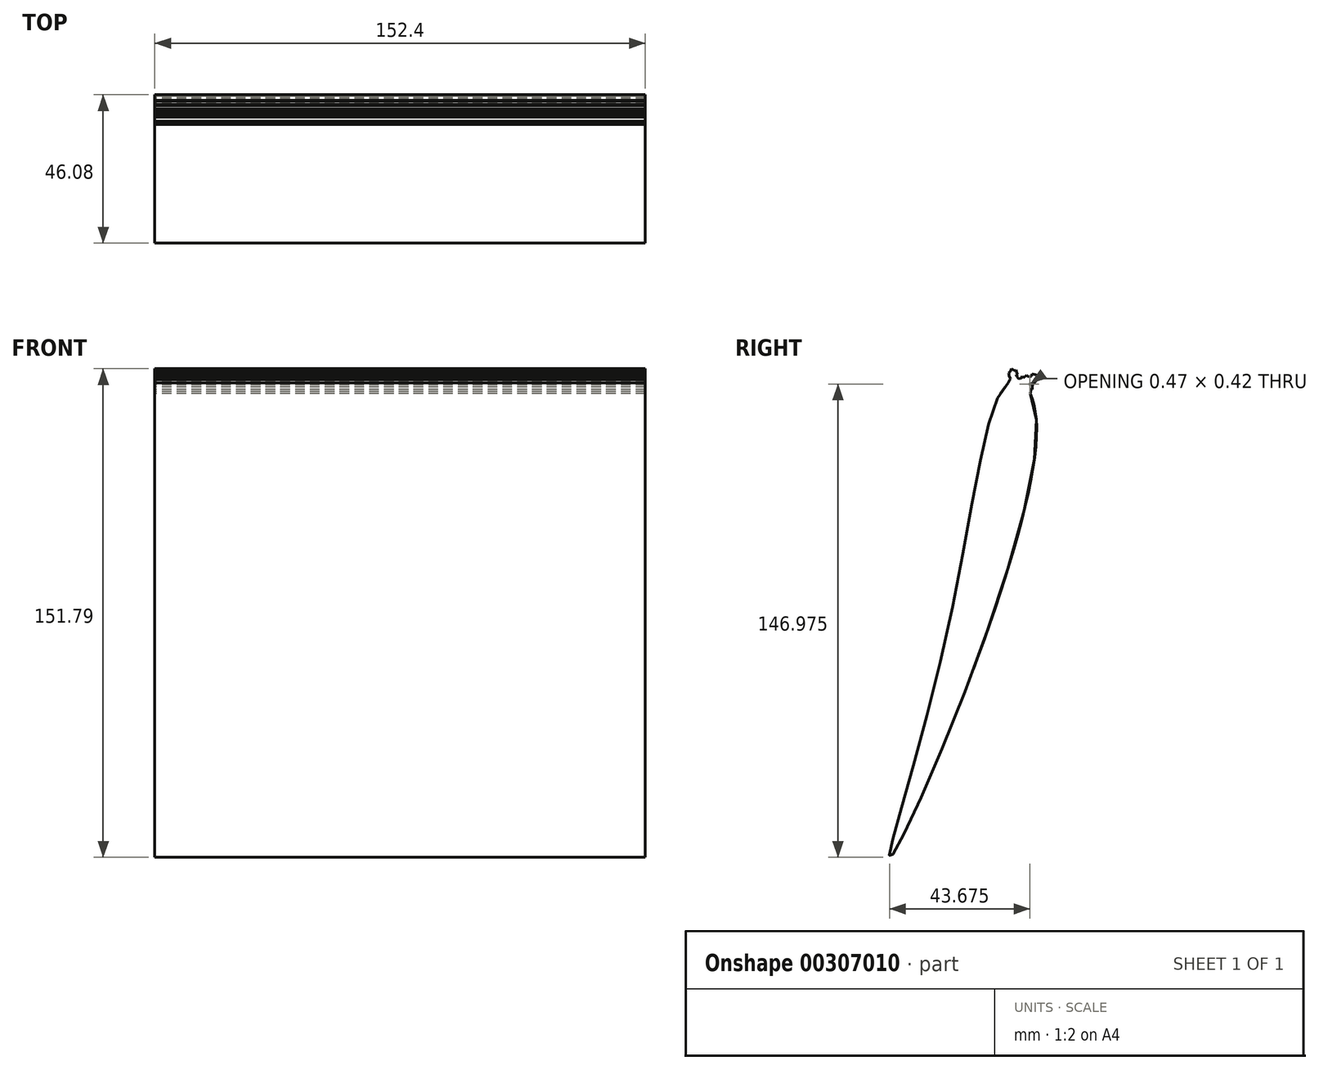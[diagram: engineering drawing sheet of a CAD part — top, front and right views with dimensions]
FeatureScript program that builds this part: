
annotation { "Feature Type Name" : "Feature", "Feature Type Description" : "" }
export const myFeature = defineFeature(function(context is Context, id is Id, definition is map)
    precondition{}
    {
        {
            var Q0;
            Q0=qCreatedBy(makeId("Right.planeOp"),FACE);
            var sketch = newSketch(context, id + "F0", { "sketchPlane" : qUnion([Q0])});
            skFitSpline(sketch, "E0", {"points": [v(34.7, 70.83) * mm, v(42.97, 55.32) * mm, v(-2.03, -76.46) * mm, v(14.34, -10.78) * mm, v(34.7, 70.83) * mm]});
            skLineSegment(sketch, "E1", {"start": v(38.76, 70.2) * mm, "end": v(41.6, 72.44) * mm});
            skLineSegment(sketch, "E2", {"start": v(41.6, 72.44) * mm, "end": v(42.47, 71.48) * mm});
            skLineSegment(sketch, "E3", {"start": v(42.47, 71.48) * mm, "end": v(39.8, 69.08) * mm});
            skLineSegment(sketch, "E4", {"start": v(39.8, 69.08) * mm, "end": v(38.76, 70.2) * mm});
            skLineSegment(sketch, "E5", {"start": v(41.6, 72.44) * mm, "end": v(42.32, 73.08) * mm});
            skPoint(sketch, "E5.endSnap0", {"position": v(42.04, 71.96) * mm});
            skLineSegment(sketch, "E6", {"start": v(42.32, 73.08) * mm, "end": v(43.12, 72.06) * mm});
            skLineSegment(sketch, "E7", {"start": v(43.12, 72.06) * mm, "end": v(42.47, 71.48) * mm});
            skLineSegment(sketch, "E8", {"start": v(36.46, 71.21) * mm, "end": v(36.05, 73.82) * mm});
            skLineSegment(sketch, "E9", {"start": v(36.05, 73.82) * mm, "end": v(34.77, 73.62) * mm});
            skLineSegment(sketch, "E10", {"start": v(34.77, 73.62) * mm, "end": v(35.17, 71.04) * mm});
            skLineSegment(sketch, "E11", {"start": v(35.17, 71.04) * mm, "end": v(36.46, 71.21) * mm});
            skLineSegment(sketch, "E12", {"start": v(40.32, 68.46) * mm, "end": v(40.67, 69.85) * mm});
            skLineSegment(sketch, "E13", {"start": v(40.67, 69.85) * mm, "end": v(41.14, 70.28) * mm});
            skLineSegment(sketch, "E14", {"start": v(41.14, 70.28) * mm, "end": v(41.08, 70.02) * mm});
            skPoint(sketch, "E14.endSnap0", {"position": v(40.9, 70.07) * mm});
            skLineSegment(sketch, "E15", {"start": v(41.08, 70.02) * mm, "end": v(40.67, 69.85) * mm});
            skLineSegment(sketch, "E16", {"start": v(40.5, 69.16) * mm, "end": v(41.26, 69.84) * mm});
            skLineSegment(sketch, "E17", {"start": v(41.26, 69.84) * mm, "end": v(41.43, 70.54) * mm});
            skLineSegment(sketch, "E18", {"start": v(41.43, 70.54) * mm, "end": v(41.8, 70.12) * mm});
            skLineSegment(sketch, "E19", {"start": v(41.8, 70.12) * mm, "end": v(41.26, 69.84) * mm});
            skLineSegment(sketch, "E20", {"start": v(42.1, 71.14) * mm, "end": v(42.93, 70.94) * mm});
            skLineSegment(sketch, "E21", {"start": v(42.93, 70.94) * mm, "end": v(42.47, 71.48) * mm});
            skLineSegment(sketch, "E22", {"start": v(43.12, 72.06) * mm, "end": v(43.03, 71.34) * mm});
            skLineSegment(sketch, "E23", {"start": v(43.03, 71.34) * mm, "end": v(42.27, 70.66) * mm});
            skLineSegment(sketch, "E24", {"start": v(42.27, 70.66) * mm, "end": v(41.43, 70.54) * mm});
            skLineSegment(sketch, "E25", {"start": v(42.27, 70.66) * mm, "end": v(42.2, 70.35) * mm});
            skLineSegment(sketch, "E26", {"start": v(42.2, 70.35) * mm, "end": v(41.8, 70.12) * mm});
            skLineSegment(sketch, "E27", {"start": v(43.03, 71.34) * mm, "end": v(42.47, 71.48) * mm});
            skLineSegment(sketch, "E28", {"start": v(41.8, 70.12) * mm, "end": v(41.57, 69.17) * mm});
            skLineSegment(sketch, "E29", {"start": v(41.57, 69.17) * mm, "end": v(40.5, 69.16) * mm});
            skLineSegment(sketch, "E30", {"start": v(43.12, 72.06) * mm, "end": v(43.31, 72.83) * mm});
            skLineSegment(sketch, "E31", {"start": v(43.31, 72.83) * mm, "end": v(42.85, 72.4) * mm});
            skLineSegment(sketch, "E32", {"start": v(42.85, 72.4) * mm, "end": v(43.31, 72.83) * mm});
            skLineSegment(sketch, "E33", {"start": v(43.31, 72.83) * mm, "end": v(42.32, 73.08) * mm});
            skLineSegment(sketch, "E34", {"start": v(42.32, 73.08) * mm, "end": v(41.52, 73.28) * mm});
            skLineSegment(sketch, "E35", {"start": v(41.52, 73.28) * mm, "end": v(41.33, 72.5) * mm});
            skLineSegment(sketch, "E36", {"start": v(41.33, 72.5) * mm, "end": v(40.33, 72.38) * mm});
            skLineSegment(sketch, "E37", {"start": v(40.33, 72.38) * mm, "end": v(39.9, 72.86) * mm});
            skLineSegment(sketch, "E38", {"start": v(39.9, 72.86) * mm, "end": v(39.62, 71.76) * mm});
            skLineSegment(sketch, "E39", {"start": v(39.62, 71.76) * mm, "end": v(39.52, 71.34) * mm});
            skLineSegment(sketch, "E40", {"start": v(39.52, 71.34) * mm, "end": v(38.78, 71.34) * mm});
            skLineSegment(sketch, "E41", {"start": v(38.78, 71.34) * mm, "end": v(38.56, 70.47) * mm});
            skLineSegment(sketch, "E42", {"start": v(38.56, 70.47) * mm, "end": v(38.76, 70.2) * mm});
            skLineSegment(sketch, "E43", {"start": v(39.9, 72.86) * mm, "end": v(38.88, 71.95) * mm});
            skLineSegment(sketch, "E44", {"start": v(38.88, 71.95) * mm, "end": v(38.39, 72.5) * mm});
            skLineSegment(sketch, "E45", {"start": v(38.39, 72.5) * mm, "end": v(37.95, 71.74) * mm});
            skLineSegment(sketch, "E46", {"start": v(37.95, 71.74) * mm, "end": v(37.25, 71.9) * mm});
            skLineSegment(sketch, "E47", {"start": v(37.25, 71.9) * mm, "end": v(36.66, 71.36) * mm});
            skLineSegment(sketch, "E48", {"start": v(37.25, 71.9) * mm, "end": v(36.73, 72.48) * mm});
            skLineSegment(sketch, "E49", {"start": v(36.73, 72.48) * mm, "end": v(36.35, 72.13) * mm});
            skLineSegment(sketch, "E50", {"start": v(36.35, 72.13) * mm, "end": v(36.55, 72.95) * mm});
            skLineSegment(sketch, "E51", {"start": v(36.55, 72.95) * mm, "end": v(36.12, 73.43) * mm});
            skLineSegment(sketch, "E52", {"start": v(36.12, 73.43) * mm, "end": v(36.05, 73.82) * mm});
            skLineSegment(sketch, "E53", {"start": v(36.55, 72.95) * mm, "end": v(36.73, 73.65) * mm});
            skLineSegment(sketch, "E54", {"start": v(36.73, 73.65) * mm, "end": v(36.12, 73.43) * mm});
            skLineSegment(sketch, "E55", {"start": v(36.73, 73.65) * mm, "end": v(37.16, 73.17) * mm});
            skLineSegment(sketch, "E56", {"start": v(37.16, 73.17) * mm, "end": v(36.55, 72.95) * mm});
            skLineSegment(sketch, "E57", {"start": v(36.73, 73.65) * mm, "end": v(36.6, 74.5) * mm});
            skLineSegment(sketch, "E58", {"start": v(36.6, 74.5) * mm, "end": v(36.05, 73.82) * mm});
            skLineSegment(sketch, "E59", {"start": v(36.05, 73.82) * mm, "end": v(35.57, 74.36) * mm});
            skPoint(sketch, "E59.endSnap0", {"position": v(35.4, 73.72) * mm});
            skLineSegment(sketch, "E60", {"start": v(35.57, 74.36) * mm, "end": v(34.77, 73.62) * mm});
            skLineSegment(sketch, "E61", {"start": v(34.77, 73.62) * mm, "end": v(35.08, 74.88) * mm});
            skLineSegment(sketch, "E62", {"start": v(35.08, 74.88) * mm, "end": v(36.32, 74.16) * mm});
            skLineSegment(sketch, "E63", {"start": v(36.32, 74.16) * mm, "end": v(36.6, 74.5) * mm});
            skLineSegment(sketch, "E64", {"start": v(34.89, 74.11) * mm, "end": v(34.24, 73.53) * mm});
            skLineSegment(sketch, "E65", {"start": v(34.24, 73.53) * mm, "end": v(35.01, 72.14) * mm});
            skLineSegment(sketch, "E66", {"start": v(35.01, 72.14) * mm, "end": v(34.4, 72.62) * mm});
            skLineSegment(sketch, "E67", {"start": v(34.4, 72.62) * mm, "end": v(34.34, 73.08) * mm});
            skLineSegment(sketch, "E68", {"start": v(34.34, 73.08) * mm, "end": v(34.24, 73.53) * mm});
            skLineSegment(sketch, "E69", {"start": v(35.17, 71.04) * mm, "end": v(34.7, 70.83) * mm});
            skLineSegment(sketch, "E70", {"start": v(34.7, 70.83) * mm, "end": v(34.59, 71.5) * mm});
            skLineSegment(sketch, "E71", {"start": v(34.59, 71.5) * mm, "end": v(35.07, 72.04) * mm});
            skLineSegment(sketch, "E72", {"start": v(35.07, 72.04) * mm, "end": v(34.4, 72.62) * mm});
            skLineSegment(sketch, "E73", {"start": v(34.4, 72.62) * mm, "end": v(34.83, 71.77) * mm});
            skLineSegment(sketch, "E74", {"start": v(41.57, 69.17) * mm, "end": v(41.58, 68.47) * mm});
            skLineSegment(sketch, "E75", {"start": v(41.58, 68.47) * mm, "end": v(41.05, 68.4) * mm});
            skLineSegment(sketch, "E76", {"start": v(41.05, 68.4) * mm, "end": v(41.13, 67.78) * mm});
            skLineSegment(sketch, "E77", {"start": v(41.13, 67.78) * mm, "end": v(40.97, 67.13) * mm});
            skLineSegment(sketch, "E78", {"start": v(40.97, 67.13) * mm, "end": v(40.32, 68.46) * mm});
            skLineSegment(sketch, "E79", {"start": v(34.59, 71.5) * mm, "end": v(34.08, 70.44) * mm});
            skLineSegment(sketch, "E80", {"start": v(34.08, 70.44) * mm, "end": v(34.7, 70.83) * mm});
            skLineSegment(sketch, "E81", {"start": v(36.55, 72.95) * mm, "end": v(36.73, 72.48) * mm});
            skLineSegment(sketch, "E82.0", {"start": v(34.59, 71.5) * mm, "end": v(41.26, 69.84) * mm, "construction": true});
            skLineSegment(sketch, "E83.0", {"start": v(34.34, 73.08) * mm, "end": v(42.93, 70.94) * mm, "construction": true});
            skLineSegment(sketch, "E84.0", {"start": v(34.4, 72.62) * mm, "end": v(37.25, 71.9) * mm, "construction": true});
            skLineSegment(sketch, "E85.0", {"start": v(35.01, 72.14) * mm, "end": v(42.2, 70.35) * mm, "construction": true});
            skLineSegment(sketch, "E86.0", {"start": v(34.24, 73.53) * mm, "end": v(43.03, 71.34) * mm, "construction": true});
            skLineSegment(sketch, "E87.0", {"start": v(35.08, 74.88) * mm, "end": v(43.31, 72.83) * mm, "construction": true});
            skLineSegment(sketch, "E88.0", {"start": v(34.89, 74.11) * mm, "end": v(43.12, 72.06) * mm, "construction": true});
            skLineSegment(sketch, "E89.0", {"start": v(36.12, 73.43) * mm, "end": v(42.04, 71.96) * mm, "construction": true});
            skLineSegment(sketch, "E90.0", {"start": v(40.9, 70.07) * mm, "end": v(41.08, 70.02) * mm, "construction": true});
            skLineSegment(sketch, "E91.0", {"start": v(38.88, 71.95) * mm, "end": v(39.62, 71.76) * mm, "construction": true});
            skLineSegment(sketch, "E92.0", {"start": v(39.52, 71.34) * mm, "end": v(42.27, 70.66) * mm, "construction": true});
            skLineSegment(sketch, "E93.0", {"start": v(35.01, 72.14) * mm, "end": v(35.57, 74.36) * mm, "construction": true});
            skLineSegment(sketch, "E94.0", {"start": v(42.27, 70.66) * mm, "end": v(42.47, 71.48) * mm, "construction": true});
            skLineSegment(sketch, "E95.0", {"start": v(34.77, 73.62) * mm, "end": v(34.89, 74.11) * mm, "construction": true});
            skLineSegment(sketch, "E96.0", {"start": v(42.04, 71.96) * mm, "end": v(42.32, 73.08) * mm, "construction": true});
            skLineSegment(sketch, "E97.0", {"start": v(40.5, 69.16) * mm, "end": v(41.52, 73.28) * mm, "construction": true});
            skLineSegment(sketch, "E98.0", {"start": v(42.93, 70.94) * mm, "end": v(43.03, 71.34) * mm, "construction": true});
            skSolve(sketch);
        }
        {
            var Q0;
            Q0=qSketchRegion(id+"F0",true);
            var Q1;
            Q1=makeQuery(id+"F0.imprint","IMPRINT",FACE,{"disambiguationData":[TD([[makeQuery(id+"F0.imprint","IMPRINT",EDGE,{"derivedFrom":sQuery(id+"F0.wireOp",EDGE,"E1")}),1.0]])]});
            var Q2;
            {var subQ3=sQuery(id+"F0.wireOp",EDGE,"E1");Q2=makeQuery(id+"F0.imprint","IMPRINT",FACE,{"disambiguationData":[TD([[makeQuery(id+"F0.imprint","IMPRINT",EDGE,{"derivedFrom":subQ3}),-1.0]])]});}
            var Q3;
            {var subQ0=sQuery(id+"F0.wireOp",EDGE,"E29");Q3=makeQuery(id+"F0.imprint","IMPRINT",FACE,{"disambiguationData":[TD([[makeQuery(id+"F0.imprint","IMPRINT",EDGE,{"derivedFrom":subQ0}),1.0]])]});}
            var Q4;
            {var subQ0=sQuery(id+"F0.wireOp",EDGE,"E78");var subQ1=sQuery(id+"F0.wireOp",EDGE,"E12");var subQ2=makeQuery(id+"F0.imprint","INTERSECT",VERTEX,{"derivedFrom":[subQ1,subQ0]});Q4=makeQuery(id+"F0.imprint","IMPRINT",FACE,{"disambiguationData":[TD([[makeQuery(id+"F0.imprint","IMPRINT",EDGE,{"disambiguationData":[TD([[subQ2,1.0]])],"derivedFrom":subQ0}),1.0]])]});}
            var Q5;
            {var subQ2=sQuery(id+"F0.wireOp",EDGE,"E8");Q5=makeQuery(id+"F0.imprint","IMPRINT",FACE,{"disambiguationData":[TD([[makeQuery(id+"F0.imprint","IMPRINT",EDGE,{"derivedFrom":subQ2}),-1.0]])]});}
            var Q6;
            {var subQ0=sQuery(id+"F0.wireOp",EDGE,"E11");Q6=makeQuery(id+"F0.imprint","IMPRINT",FACE,{"disambiguationData":[TD([[makeQuery(id+"F0.imprint","IMPRINT",EDGE,{"derivedFrom":subQ0}),1.0]])]});}
            var Q7;
            {var subQ0=sQuery(id+"F0.wireOp",EDGE,"E4");Q7=makeQuery(id+"F0.imprint","IMPRINT",FACE,{"disambiguationData":[TD([[makeQuery(id+"F0.imprint","IMPRINT",EDGE,{"derivedFrom":subQ0}),-1.0]])]});}
            var Q8;
            {var subQ0=sQuery(id+"F0.wireOp",EDGE,"E78");var subQ1=sQuery(id+"F0.wireOp",EDGE,"E0");var subQ3=makeQuery(id+"F0.imprint","INTERSECT",VERTEX,{"derivedFrom":[subQ1,subQ0]});Q8=makeQuery(id+"F0.imprint","IMPRINT",FACE,{"disambiguationData":[TD([[makeQuery(id+"F0.imprint","IMPRINT",EDGE,{"disambiguationData":[TD([[subQ3,-1.0]])],"derivedFrom":subQ1}),-1.0]])]});}
            var Q9;
            {var subQ6=sQuery(id+"F0.wireOp",EDGE,"E8");Q9=makeQuery(id+"F0.imprint","IMPRINT",FACE,{"disambiguationData":[TD([[makeQuery(id+"F0.imprint","IMPRINT",EDGE,{"derivedFrom":subQ6}),1.0]])]});}
            var Q10;
            Q10=makeQuery(id+"F0.imprint","IMPRINT",FACE,{"disambiguationData":[TD([[makeQuery(id+"F0.imprint","IMPRINT",EDGE,{"derivedFrom":sQuery(id+"F0.wireOp",EDGE,"E58")}),-1.0]])]});
            var Q11;
            {var subQ0=sQuery(id+"F0.wireOp",EDGE,"E69");Q11=makeQuery(id+"F0.imprint","IMPRINT",FACE,{"disambiguationData":[TD([[makeQuery(id+"F0.imprint","IMPRINT",EDGE,{"derivedFrom":subQ0}),-1.0]])]});}
            var Q12;
            {var subQ1=sQuery(id+"F0.wireOp",EDGE,"E70");Q12=makeQuery(id+"F0.imprint","IMPRINT",FACE,{"disambiguationData":[TD([[makeQuery(id+"F0.imprint","IMPRINT",EDGE,{"derivedFrom":subQ1}),1.0]])]});}
            var Q13;
            {var subQ0=sQuery(id+"F0.wireOp",EDGE,"E80");Q13=makeQuery(id+"F0.imprint","IMPRINT",FACE,{"disambiguationData":[TD([[makeQuery(id+"F0.imprint","IMPRINT",EDGE,{"derivedFrom":subQ0}),1.0]])]});}
            var Q14;
            {var subQ5=sQuery(id+"F0.wireOp",EDGE,"E64");Q14=makeQuery(id+"F0.imprint","IMPRINT",FACE,{"disambiguationData":[TD([[makeQuery(id+"F0.imprint","IMPRINT",EDGE,{"derivedFrom":subQ5}),1.0]])]});}
            var Q15;
            {var subQ1=sQuery(id+"F0.wireOp",EDGE,"E70");Q15=makeQuery(id+"F0.imprint","IMPRINT",FACE,{"disambiguationData":[TD([[makeQuery(id+"F0.imprint","IMPRINT",EDGE,{"derivedFrom":subQ1}),-1.0]])]});}
            var Q16;
            {var subQ0=sQuery(id+"F0.wireOp",EDGE,"E67");Q16=makeQuery(id+"F0.imprint","IMPRINT",FACE,{"disambiguationData":[TD([[makeQuery(id+"F0.imprint","IMPRINT",EDGE,{"derivedFrom":subQ0}),-1.0]])]});}
            var Q17;
            {var subQ0=sQuery(id+"F0.wireOp",EDGE,"E72");var subQ1=sQuery(id+"F0.wireOp",EDGE,"E10");var subQ2=makeQuery(id+"F0.imprint","INTERSECT",VERTEX,{"derivedFrom":[subQ1,subQ0]});Q17=makeQuery(id+"F0.imprint","IMPRINT",FACE,{"disambiguationData":[TD([[makeQuery(id+"F0.imprint","IMPRINT",EDGE,{"disambiguationData":[TD([[subQ2,-1.0]])],"derivedFrom":subQ1}),1.0]])]});}
            var Q18;
            Q18=makeQuery(id+"F0.imprint","IMPRINT",FACE,{"disambiguationData":[TD([[makeQuery(id+"F0.imprint","IMPRINT",EDGE,{"derivedFrom":sQuery(id+"F0.wireOp",EDGE,"E9")}),-1.0]])]});
            var Q19;
            Q19=makeQuery(id+"F0.imprint","IMPRINT",FACE,{"disambiguationData":[TD([[makeQuery(id+"F0.imprint","IMPRINT",EDGE,{"derivedFrom":sQuery(id+"F0.wireOp",EDGE,"E17")}),-1.0]])]});
            var Q20;
            {var subQ0=sQuery(id+"F0.wireOp",EDGE,"E65");var subQ1=sQuery(id+"F0.wireOp",EDGE,"E10");var subQ2=makeQuery(id+"F0.imprint","INTERSECT",VERTEX,{"derivedFrom":[subQ1,subQ0]});Q20=makeQuery(id+"F0.imprint","IMPRINT",FACE,{"disambiguationData":[TD([[makeQuery(id+"F0.imprint","IMPRINT",EDGE,{"disambiguationData":[TD([[subQ2,-1.0]])],"derivedFrom":subQ1}),1.0]])]});}
            var Q21;
            Q21=makeQuery(id+"F0.imprint","IMPRINT",FACE,{"disambiguationData":[TD([[makeQuery(id+"F0.imprint","IMPRINT",EDGE,{"derivedFrom":sQuery(id+"F0.wireOp",EDGE,"E18")}),1.0]])]});
            var Q22;
            Q22=makeQuery(id+"F0.imprint","IMPRINT",FACE,{"disambiguationData":[TD([[makeQuery(id+"F0.imprint","IMPRINT",EDGE,{"derivedFrom":sQuery(id+"F0.wireOp",EDGE,"E49")}),-1.0]])]});
            var Q23;
            {var subQ2=sQuery(id+"F0.wireOp",EDGE,"E32");Q23=makeQuery(id+"F0.imprint","IMPRINT",FACE,{"disambiguationData":[TD([[makeQuery(id+"F0.imprint","IMPRINT",EDGE,{"derivedFrom":subQ2}),1.0]])]});}
            var Q24;
            {var subQ0=sQuery(id+"F0.wireOp",EDGE,"E66");var subQ1=sQuery(id+"F0.wireOp",EDGE,"E10");var subQ2=makeQuery(id+"F0.imprint","INTERSECT",VERTEX,{"derivedFrom":[subQ1,subQ0]});Q24=makeQuery(id+"F0.imprint","IMPRINT",FACE,{"disambiguationData":[TD([[makeQuery(id+"F0.imprint","IMPRINT",EDGE,{"disambiguationData":[TD([[subQ2,-1.0]])],"derivedFrom":subQ1}),-1.0]])]});}
            var Q25;
            Q25=makeQuery(id+"F0.imprint","IMPRINT",FACE,{"disambiguationData":[TD([[makeQuery(id+"F0.imprint","IMPRINT",EDGE,{"derivedFrom":sQuery(id+"F0.wireOp",EDGE,"E2")}),1.0]])]});
            var Q26;
            {var subQ5=sQuery(id+"F0.wireOp",EDGE,"E73");Q26=makeQuery(id+"F0.imprint","IMPRINT",FACE,{"disambiguationData":[TD([[makeQuery(id+"F0.imprint","IMPRINT",EDGE,{"derivedFrom":subQ5}),1.0]])]});}
            var Q27;
            {var subQ1=sQuery(id+"F0.wireOp",EDGE,"E14");Q27=makeQuery(id+"F0.imprint","IMPRINT",FACE,{"disambiguationData":[TD([[makeQuery(id+"F0.imprint","IMPRINT",EDGE,{"derivedFrom":subQ1}),1.0]])]});}
            var Q28;
            Q28=makeQuery(id+"F0.imprint","IMPRINT",FACE,{"disambiguationData":[TD([[makeQuery(id+"F0.imprint","IMPRINT",EDGE,{"derivedFrom":sQuery(id+"F0.wireOp",EDGE,"E16")}),-1.0]])]});
            var Q29;
            {var subQ0=sQuery(id+"F0.wireOp",EDGE,"E24");Q29=makeQuery(id+"F0.imprint","IMPRINT",FACE,{"disambiguationData":[TD([[makeQuery(id+"F0.imprint","IMPRINT",EDGE,{"derivedFrom":subQ0}),-1.0]])]});}
            var Q30;
            Q30=makeQuery(id+"F0.imprint","IMPRINT",FACE,{"disambiguationData":[TD([[makeQuery(id+"F0.imprint","IMPRINT",EDGE,{"derivedFrom":sQuery(id+"F0.wireOp",EDGE,"E13")}),-1.0]])]});
            var Q31;
            {var subQ0=sQuery(id+"F0.wireOp",EDGE,"E21");var subQ1=sQuery(id+"F0.wireOp",EDGE,"E20");var subQ2=makeQuery(id+"F0.imprint","INTERSECT",VERTEX,{"derivedFrom":[subQ1,subQ0]});Q31=makeQuery(id+"F0.imprint","IMPRINT",FACE,{"disambiguationData":[TD([[makeQuery(id+"F0.imprint","IMPRINT",EDGE,{"disambiguationData":[TD([[subQ2,1.0]])],"derivedFrom":subQ1}),1.0]])]});}
            var Q32;
            Q32=makeQuery(id+"F0.imprint","IMPRINT",FACE,{"disambiguationData":[TD([[makeQuery(id+"F0.imprint","IMPRINT",EDGE,{"derivedFrom":sQuery(id+"F0.wireOp",EDGE,"E53")}),-1.0]])]});
            var Q33;
            {var subQ0=sQuery(id+"F0.wireOp",EDGE,"E30");Q33=makeQuery(id+"F0.imprint","IMPRINT",FACE,{"disambiguationData":[TD([[makeQuery(id+"F0.imprint","IMPRINT",EDGE,{"derivedFrom":subQ0}),1.0]])]});}
            var Q34;
            Q34=makeQuery(id+"F0.imprint","IMPRINT",FACE,{"disambiguationData":[TD([[makeQuery(id+"F0.imprint","IMPRINT",EDGE,{"derivedFrom":sQuery(id+"F0.wireOp",EDGE,"E7")}),1.0]])]});
            var Q35;
            Q35=makeQuery(id+"F0.imprint","IMPRINT",FACE,{"disambiguationData":[TD([[makeQuery(id+"F0.imprint","IMPRINT",EDGE,{"derivedFrom":sQuery(id+"F0.wireOp",EDGE,"E51")}),-1.0]])]});
            var Q36;
            Q36=makeQuery(id+"F0.imprint","IMPRINT",FACE,{"disambiguationData":[TD([[makeQuery(id+"F0.imprint","IMPRINT",EDGE,{"derivedFrom":sQuery(id+"F0.wireOp",EDGE,"E52")}),-1.0]])]});
            var Q37;
            {var subQ1=sQuery(id+"F0.wireOp",EDGE,"E3");var subQ3=sQuery(id+"F0.wireOp",EDGE,"E20");var subQ4=makeQuery(id+"F0.imprint","INTERSECT",VERTEX,{"derivedFrom":[subQ1,subQ3]});Q37=makeQuery(id+"F0.imprint","IMPRINT",FACE,{"disambiguationData":[TD([[makeQuery(id+"F0.imprint","IMPRINT",EDGE,{"disambiguationData":[TD([[subQ4,-1.0]])],"derivedFrom":subQ3}),1.0]])]});}
            var Q38;
            {var subQ0=sQuery(id+"F0.wireOp",EDGE,"E27");Q38=makeQuery(id+"F0.imprint","IMPRINT",FACE,{"disambiguationData":[TD([[makeQuery(id+"F0.imprint","IMPRINT",EDGE,{"derivedFrom":subQ0}),1.0]])]});}
            var Q39;
            {var subQ4=sQuery(id+"F0.wireOp",EDGE,"E4");Q39=makeQuery(id+"F0.imprint","IMPRINT",FACE,{"disambiguationData":[TD([[makeQuery(id+"F0.imprint","IMPRINT",EDGE,{"derivedFrom":subQ4}),1.0]])]});}
            extrude(context, id + "F1", {"entities" : qUnion([Q0, Q1, Q2, Q3, Q4, Q5, Q6, Q7, Q8, Q9, Q10, Q11, Q12, Q13, Q14, Q15, Q16, Q17, Q18, Q19, Q20, Q21, Q22, Q23, Q24, Q25, Q26, Q27, Q28, Q29, Q30, Q31, Q32, Q33, Q34, Q35, Q36, Q37, Q38, Q39]), "depth" : 76.2 * mm, "hasSecondDirection" : true, "secondDirectionOppositeDirection" : true, "secondDirectionDepth" : 76.2 * mm});
        }
    });
